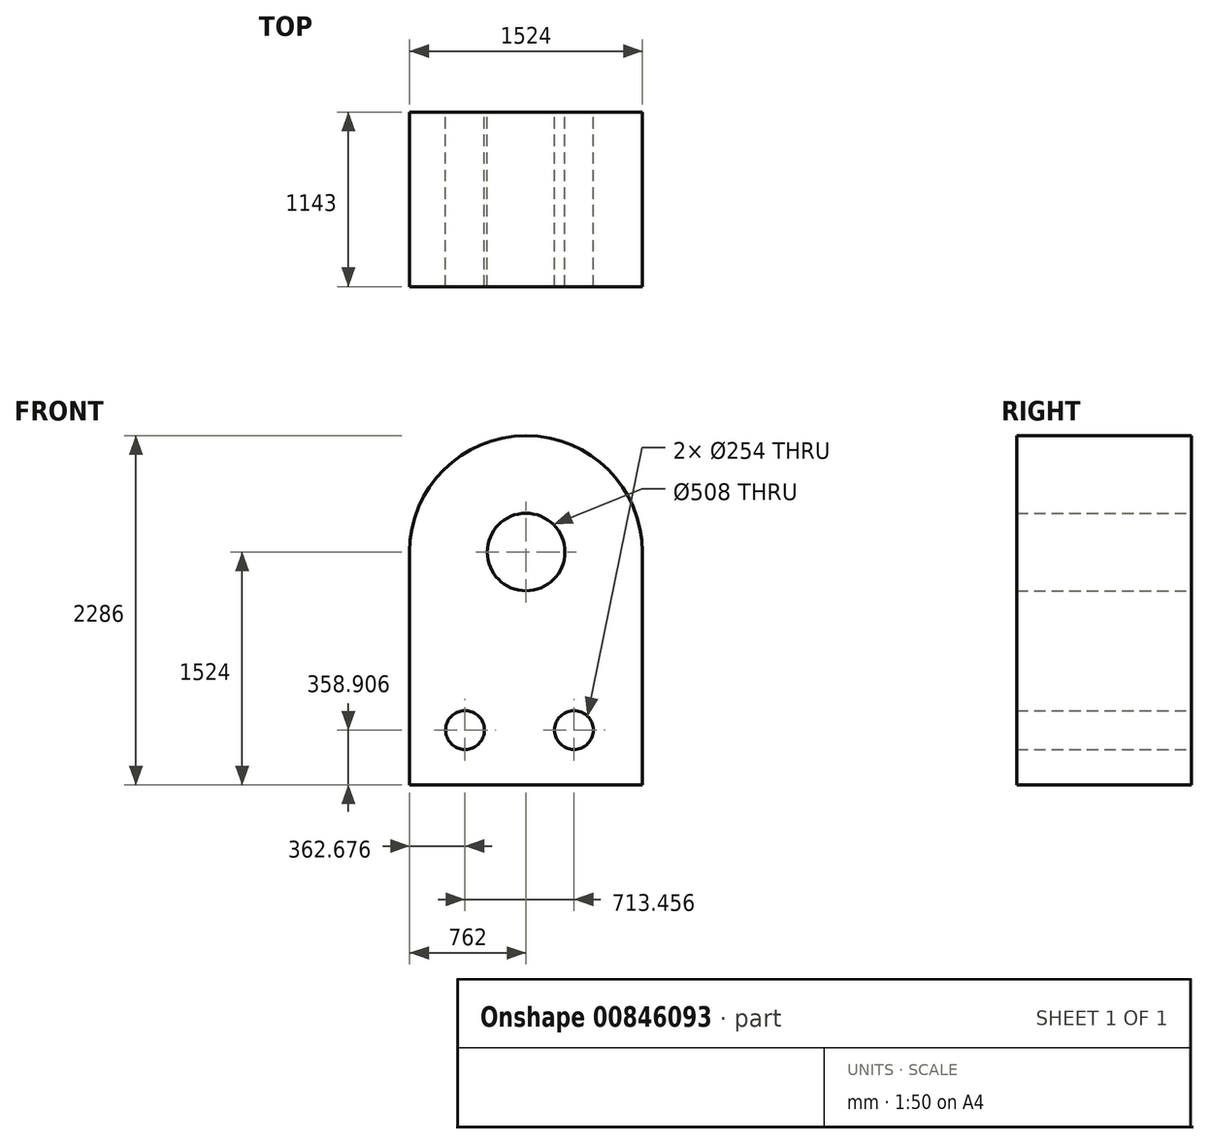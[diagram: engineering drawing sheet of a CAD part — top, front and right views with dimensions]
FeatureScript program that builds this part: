
annotation { "Feature Type Name" : "Feature", "Feature Type Description" : "" }
export const myFeature = defineFeature(function(context is Context, id is Id, definition is map)
    precondition{}
    {
        {
            var Q0;
            Q0=qCreatedBy(makeId("Front.planeOp"),FACE);
            var sketch = newSketch(context, id + "F0", { "sketchPlane" : qUnion([Q0])});
            skLineSegment(sketch, "E0", {"start": v(127, 0) * mm, "end": v(1397, 0) * mm});
            skLineSegment(sketch, "E1", {"start": v(1524, 127) * mm, "end": v(1524, 1524) * mm});
            skLineSegment(sketch, "E2", {"start": v(0, 127) * mm, "end": v(0, 1524) * mm});
            skCircle(sketch, "E3", {"center": v(762, 1524) * mm, "radius": 254 * mm});
            skPoint(sketch, "E3.centerSnap0", {"position": v(762, 0) * mm});
            skArc(sketch, "E4", {"start": v(1270, 1524) * mm, "mid": v(762, 2032) * mm, "end": v(254, 1524) * mm});
            skArc(sketch, "E5", {"start": v(1524, 1524) * mm, "mid": v(762, 2286) * mm, "end": v(0, 1524) * mm});
            skPoint(sketch, "E6.orphan", {"position": v(0, 0) * mm});
            skPoint(sketch, "E7.orphan", {"position": v(1524, 0) * mm});
            skCircle(sketch, "E8", {"center": v(362.68, 358.9) * mm, "radius": 127 * mm});
            skCircle(sketch, "E9", {"center": v(1076.13, 358.9) * mm, "radius": 127 * mm});
            skLineSegment(sketch, "E10", {"start": v(254, 1524) * mm, "end": v(0, 1524) * mm});
            skLineSegment(sketch, "E11", {"start": v(1524, 1524) * mm, "end": v(1270, 1524) * mm});
            skLineSegment(sketch, "E12", {"start": v(0, 127) * mm, "end": v(0, 0) * mm});
            skLineSegment(sketch, "E13", {"start": v(127, 0) * mm, "end": v(0, 0) * mm});
            skLineSegment(sketch, "E14", {"start": v(1524, 127) * mm, "end": v(1524, 0) * mm});
            skLineSegment(sketch, "E15", {"start": v(1397, 0) * mm, "end": v(1524, 0) * mm});
            skLineSegment(sketch, "E16", {"start": v(1524, 127) * mm, "end": v(1397, 127) * mm});
            skLineSegment(sketch, "E17", {"start": v(1397, 127) * mm, "end": v(1397, 0) * mm});
            skLineSegment(sketch, "E18", {"start": v(127, 0) * mm, "end": v(127, 127) * mm});
            skLineSegment(sketch, "E19", {"start": v(127, 127) * mm, "end": v(0, 127) * mm});
            skSolve(sketch);
        }
        {
            var Q0;
            Q0 = qSketchRegion(id + "F0", true);
            extrude(context, id + "F1", {"entities" : qUnion([Q0]), "depth" : 1143 * mm, "offsetDistance" : 25.4 * mm});
        }
        {
            var Q0;
            Q0=makeQuery(id+"F0.imprint","IMPRINT",FACE,{"disambiguationData":[TD([[makeQuery(id+"F0.imprint","IMPRINT",EDGE,{"derivedFrom":sQuery(id+"F0.wireOp",EDGE,"E14")}),-1.0]])]});
            var Q1;
            Q1=makeQuery(id+"F0.imprint","IMPRINT",FACE,{"disambiguationData":[TD([[makeQuery(id+"F0.imprint","IMPRINT",EDGE,{"derivedFrom":sQuery(id+"F0.wireOp",EDGE,"E12")}),1.0]])]});
            extrude(context, id + "F2", {"entities" : qUnion([Q0, Q1]), "operationType" : NewBodyOperationType.REMOVE, "oppositeDirection" : true, "depth" : 635 * mm, "offsetDistance" : 25.4 * mm});
        }
    });
